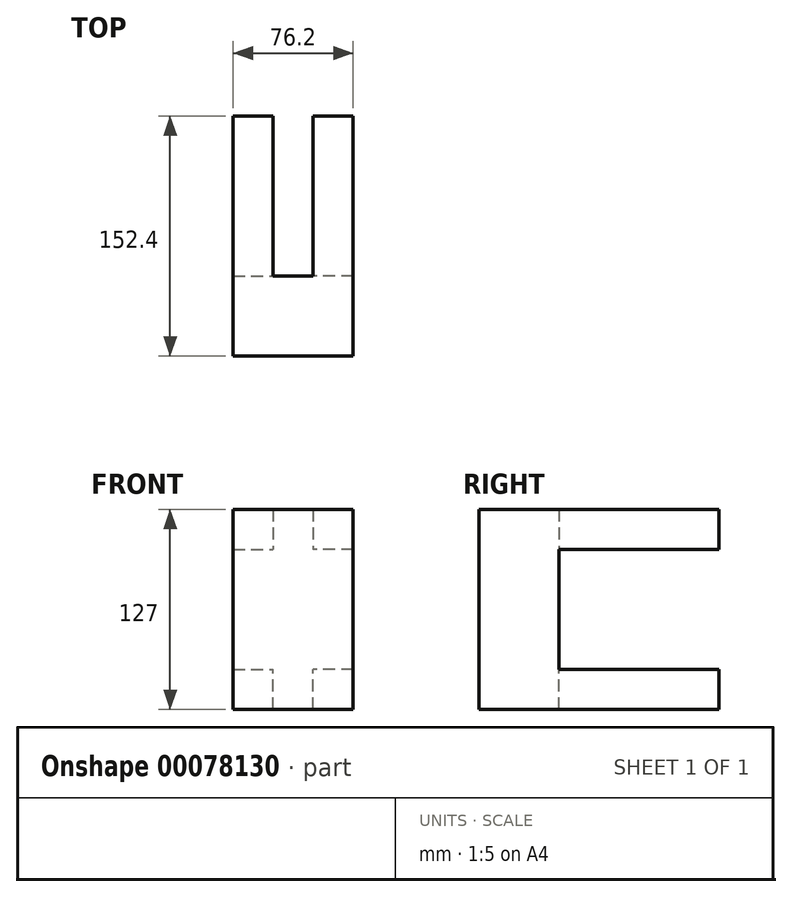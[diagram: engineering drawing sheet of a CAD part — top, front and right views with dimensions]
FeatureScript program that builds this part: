
annotation { "Feature Type Name" : "Feature", "Feature Type Description" : "" }
export const myFeature = defineFeature(function(context is Context, id is Id, definition is map)
    precondition{}
    {
        {
            var Q0;
            Q0=qCreatedBy(makeId("Front.planeOp"),FACE);
            var sketch = newSketch(context, id + "F0", { "sketchPlane" : qUnion([Q0])});
            skLineSegment(sketch, "E0.bottom", {"start": v(38.1, 63.5) * mm, "end": v(-38.1, 63.5) * mm});
            skLineSegment(sketch, "E0.top", {"start": v(38.1, -63.5) * mm, "end": v(-38.1, -63.5) * mm});
            skLineSegment(sketch, "E0.left", {"start": v(38.1, 63.5) * mm, "end": v(38.1, -63.5) * mm});
            skLineSegment(sketch, "E0.right", {"start": v(-38.1, 63.5) * mm, "end": v(-38.1, -63.5) * mm});
            skPoint(sketch, "E0.middle", {"position": v(0, 0) * mm});
            skSolve(sketch);
        }
        {
            var Q0;
            Q0 = qSketchRegion(id + "F0", true);
            extrude(context, id + "F1", {"entities" : qUnion([Q0]), "depth" : 50.8 * mm});
        }
        {
            var Q0;
            Q0=makeQuery(id+"F1.opExtrude","CAP_FACE",FACE,{"disambiguationData":[OSD([sQuery(id+"F0.wireOp",EDGE,"E0.bottom"),sQuery(id+"F0.wireOp",EDGE,"E0.top"),sQuery(id+"F0.wireOp",EDGE,"E0.left"),sQuery(id+"F0.wireOp",EDGE,"E0.right")])],"isStart":true});
            var sketch = newSketch(context, id + "F2", { "sketchPlane" : qUnion([Q0])});
            skLineSegment(sketch, "E1.bottom", {"start": v(38.1, 63.5) * mm, "end": v(12.7, 63.5) * mm});
            skLineSegment(sketch, "E1.top", {"start": v(38.1, 38.1) * mm, "end": v(12.7, 38.1) * mm});
            skLineSegment(sketch, "E1.left", {"start": v(38.1, 63.5) * mm, "end": v(38.1, 38.1) * mm});
            skLineSegment(sketch, "E1.right", {"start": v(12.7, 63.5) * mm, "end": v(12.7, 38.1) * mm});
            skLineSegment(sketch, "E2.bottom", {"start": v(-38.1, 63.5) * mm, "end": v(-12.7, 63.5) * mm});
            skLineSegment(sketch, "E2.top", {"start": v(-38.1, 38.1) * mm, "end": v(-12.7, 38.1) * mm});
            skLineSegment(sketch, "E2.left", {"start": v(-38.1, 63.5) * mm, "end": v(-38.1, 38.1) * mm});
            skLineSegment(sketch, "E2.right", {"start": v(-12.7, 63.5) * mm, "end": v(-12.7, 38.1) * mm});
            skLineSegment(sketch, "E3.bottom", {"start": v(38.1, -63.5) * mm, "end": v(12.7, -63.5) * mm});
            skLineSegment(sketch, "E3.top", {"start": v(38.1, -38.1) * mm, "end": v(12.7, -38.1) * mm});
            skLineSegment(sketch, "E3.left", {"start": v(38.1, -63.5) * mm, "end": v(38.1, -38.1) * mm});
            skLineSegment(sketch, "E3.right", {"start": v(12.7, -63.5) * mm, "end": v(12.7, -38.1) * mm});
            skLineSegment(sketch, "E4.bottom", {"start": v(-38.1, -63.5) * mm, "end": v(-12.7, -63.5) * mm});
            skLineSegment(sketch, "E4.top", {"start": v(-38.1, -38.1) * mm, "end": v(-12.7, -38.1) * mm});
            skLineSegment(sketch, "E4.left", {"start": v(-38.1, -63.5) * mm, "end": v(-38.1, -38.1) * mm});
            skLineSegment(sketch, "E4.right", {"start": v(-12.7, -63.5) * mm, "end": v(-12.7, -38.1) * mm});
            skSolve(sketch);
        }
        {
            var Q0;
            Q0=makeQuery(id+"F2.imprint","IMPRINT",FACE,{"disambiguationData":[TD([[makeQuery(id+"F2.imprint","IMPRINT",EDGE,{"derivedFrom":sQuery(id+"F2.wireOp",EDGE,"E2.bottom")}),-1.0]])]});
            extrude(context, id + "F3", {"entities" : qUnion([Q0]), "operationType" : NewBodyOperationType.ADD, "depth" : 101.6 * mm});
        }
        {
            var Q0;
            Q0 = qSketchRegion(id + "F2", true);
            extrude(context, id + "F4", {"entities" : qUnion([Q0]), "operationType" : NewBodyOperationType.ADD, "depth" : 101.6 * mm});
        }
    });
